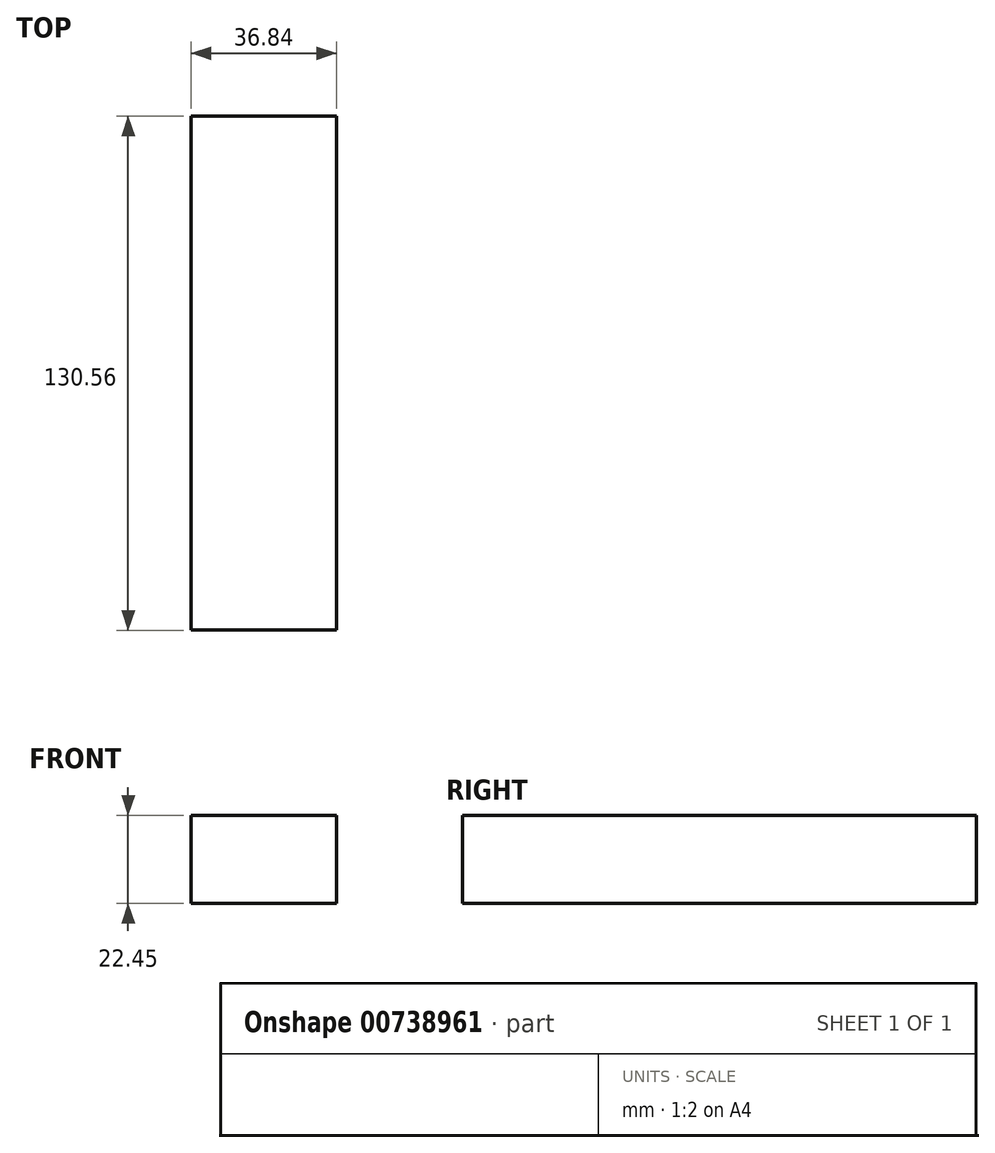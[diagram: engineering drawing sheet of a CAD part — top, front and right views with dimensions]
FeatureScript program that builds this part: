
annotation { "Feature Type Name" : "Feature", "Feature Type Description" : "" }
export const myFeature = defineFeature(function(context is Context, id is Id, definition is map)
    precondition{}
    {
        {
            var Q0;
            Q0=qCreatedBy(makeId("Front.planeOp"),FACE);
            var sketch = newSketch(context, id + "F0", { "sketchPlane" : qUnion([Q0])});
            skLineSegment(sketch, "E0.bottom", {"start": v(-71.13, 54.86) * mm, "end": v(-34.29, 54.86) * mm});
            skLineSegment(sketch, "E0.top", {"start": v(-71.13, 32.4) * mm, "end": v(-34.29, 32.4) * mm});
            skLineSegment(sketch, "E0.left", {"start": v(-71.13, 54.86) * mm, "end": v(-71.13, 32.4) * mm});
            skLineSegment(sketch, "E0.right", {"start": v(-34.29, 54.86) * mm, "end": v(-34.29, 32.4) * mm});
            skSolve(sketch);
        }
        {
            var Q0;
            Q0 = qSketchRegion(id + "F0", true);
            extrude(context, id + "F1", {"entities" : qUnion([Q0]), "endBound" : BoundingType.SYMMETRIC, "depth" : 117.86 * mm, "offsetDistance" : 25.4 * mm});
        }
        {
            var Q0;
            Q0=makeQuery(id+"F1.opExtrude","CAP_FACE",FACE,{"disambiguationData":[OSD([sQuery(id+"F0.wireOp",EDGE,"E0.bottom"),sQuery(id+"F0.wireOp",EDGE,"E0.top"),sQuery(id+"F0.wireOp",EDGE,"E0.left"),sQuery(id+"F0.wireOp",EDGE,"E0.right")])],"isStart":false});
            var sketch = newSketch(context, id + "F2", { "sketchPlane" : qUnion([Q0])});
            skSolve(sketch);
        }
        {
            var Q0;
            Q0=makeQuery(id+"F2.imprint","IMPRINT",FACE,{"disambiguationData":[TD([[makeQuery(id+"F2.imprint","IMPRINT",EDGE,{"derivedFrom":makeQuery(id+"F1.opExtrude","CAP_EDGE",EDGE,{"disambiguationData":[OSD([sQuery(id+"F0.wireOp",EDGE,"E0.bottom")])],"isStart":false})}),-1.0]])]});
            extrude(context, id + "F3", {"entities" : qUnion([Q0]), "operationType" : NewBodyOperationType.ADD, "endBound" : BoundingType.SYMMETRIC, "depth" : 25.4 * mm, "offsetDistance" : 25.4 * mm});
        }
    });
